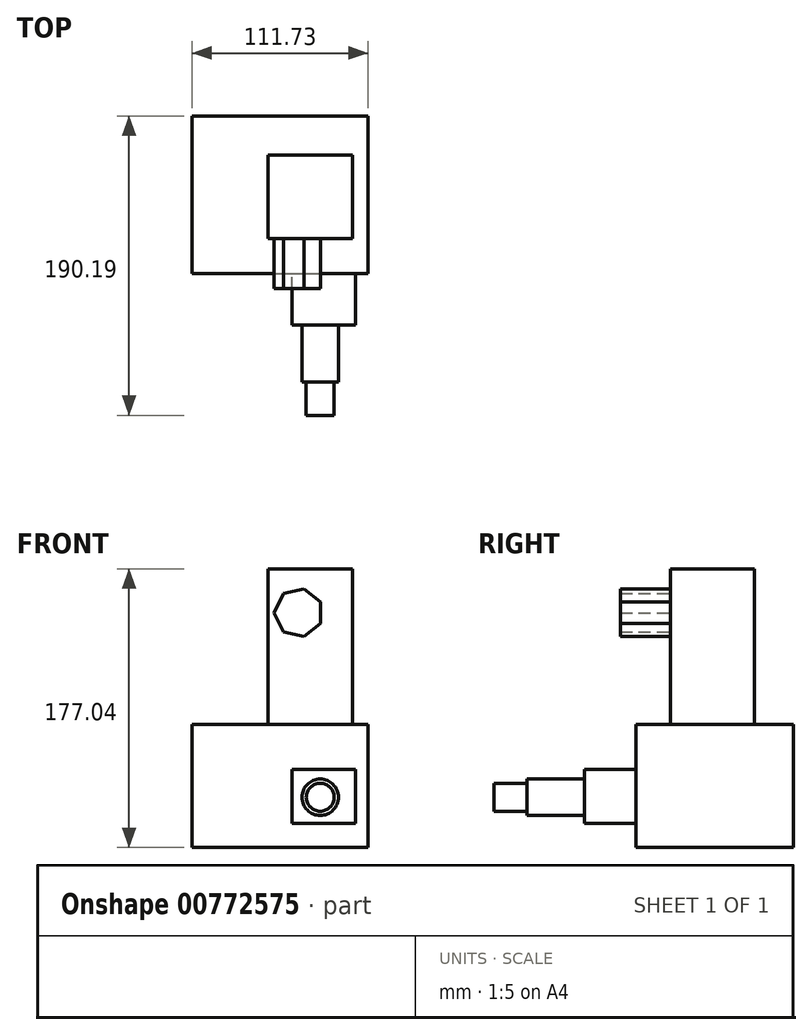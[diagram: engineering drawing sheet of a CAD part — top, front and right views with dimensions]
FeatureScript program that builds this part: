
annotation { "Feature Type Name" : "Feature", "Feature Type Description" : "" }
export const myFeature = defineFeature(function(context is Context, id is Id, definition is map)
    precondition{}
    {
        {
            var Q0;
            Q0=qCreatedBy(makeId("Top.planeOp"),FACE);
            var sketch = newSketch(context, id + "F0", { "sketchPlane" : qUnion([Q0])});
            skLineSegment(sketch, "E0.bottom", {"start": v(-56.46, -33.14) * mm, "end": v(55.27, -33.14) * mm});
            skLineSegment(sketch, "E0.top", {"start": v(-56.46, 66.88) * mm, "end": v(55.27, 66.88) * mm});
            skLineSegment(sketch, "E0.left", {"start": v(-56.46, -33.14) * mm, "end": v(-56.46, 66.88) * mm});
            skLineSegment(sketch, "E0.right", {"start": v(55.27, -33.14) * mm, "end": v(55.27, 66.88) * mm});
            skSolve(sketch);
        }
        {
            var Q0;
            Q0 = qSketchRegion(id + "F0", true);
            extrude(context, id + "F1", {"entities" : qUnion([Q0]), "depth" : 78.23 * mm, "offsetDistance" : 25.4 * mm});
        }
        {
            var Q0;
            Q0=makeQuery(id+"F1.opExtrude","SWEPT_FACE",FACE,{"disambiguationData":[OSD([sQuery(id+"F0.wireOp",EDGE,"E0.bottom")])]});
            var sketch = newSketch(context, id + "F2", { "sketchPlane" : qUnion([Q0])});
            skLineSegment(sketch, "E1.bottom", {"start": v(7.16, 49.63) * mm, "end": v(47.4, 49.63) * mm});
            skLineSegment(sketch, "E1.top", {"start": v(7.16, 15.5) * mm, "end": v(47.4, 15.5) * mm});
            skLineSegment(sketch, "E1.left", {"start": v(7.16, 49.63) * mm, "end": v(7.16, 15.5) * mm});
            skLineSegment(sketch, "E1.right", {"start": v(47.4, 49.63) * mm, "end": v(47.4, 15.5) * mm});
            skSolve(sketch);
        }
        {
            var Q0;
            Q0 = qSketchRegion(id + "F2", true);
            extrude(context, id + "F3", {"entities" : qUnion([Q0]), "operationType" : NewBodyOperationType.ADD, "depth" : 32.77 * mm, "offsetDistance" : 25.4 * mm});
        }
        {
            var Q0;
            Q0=makeQuery(id+"F3.opExtrude","CAP_FACE",FACE,{"disambiguationData":[OSD([sQuery(id+"F2.wireOp",EDGE,"E1.bottom"),sQuery(id+"F2.wireOp",EDGE,"E1.top"),sQuery(id+"F2.wireOp",EDGE,"E1.left"),sQuery(id+"F2.wireOp",EDGE,"E1.right")])],"isStart":false});
            var sketch = newSketch(context, id + "F4", { "sketchPlane" : qUnion([Q0])});
            skCircle(sketch, "E2", {"center": v(24.92, 31.95) * mm, "radius": 11.57 * mm});
            skSolve(sketch);
        }
        {
            var Q0;
            Q0 = qSketchRegion(id + "F4", true);
            extrude(context, id + "F5", {"entities" : qUnion([Q0]), "operationType" : NewBodyOperationType.ADD, "depth" : 36.32 * mm, "offsetDistance" : 25.4 * mm});
        }
        {
            var Q0;
            Q0=makeQuery(id+"F5.opExtrude","CAP_FACE",FACE,{"disambiguationData":[OSD([sQuery(id+"F4.wireOp",EDGE,"E2")])],"isStart":false});
            var sketch = newSketch(context, id + "F6", { "sketchPlane" : qUnion([Q0])});
            skCircle(sketch, "E3", {"center": v(24.92, 31.95) * mm, "radius": 8.88 * mm});
            skSolve(sketch);
        }
        {
            var Q0;
            Q0 = qSketchRegion(id + "F6", true);
            extrude(context, id + "F7", {"entities" : qUnion([Q0]), "operationType" : NewBodyOperationType.ADD, "depth" : 21.08 * mm, "offsetDistance" : 25.4 * mm});
        }
        {
            var Q0;
            Q0=makeQuery(id+"F1.opExtrude","CAP_FACE",FACE,{"disambiguationData":[OSD([sQuery(id+"F0.wireOp",EDGE,"E0.bottom"),sQuery(id+"F0.wireOp",EDGE,"E0.top"),sQuery(id+"F0.wireOp",EDGE,"E0.left"),sQuery(id+"F0.wireOp",EDGE,"E0.right")])],"isStart":false});
            var sketch = newSketch(context, id + "F8", { "sketchPlane" : qUnion([Q0])});
            skLineSegment(sketch, "E4.bottom", {"start": v(-8.07, 42) * mm, "end": v(45.48, 42) * mm});
            skLineSegment(sketch, "E4.top", {"start": v(-8.07, -11.15) * mm, "end": v(45.48, -11.15) * mm});
            skLineSegment(sketch, "E4.left", {"start": v(-8.07, 42) * mm, "end": v(-8.07, -11.15) * mm});
            skLineSegment(sketch, "E4.right", {"start": v(45.48, 42) * mm, "end": v(45.48, -11.15) * mm});
            skSolve(sketch);
        }
        {
            var Q0;
            Q0 = qSketchRegion(id + "F8", true);
            extrude(context, id + "F9", {"entities" : qUnion([Q0]), "operationType" : NewBodyOperationType.ADD, "depth" : 38.86 * mm, "offsetDistance" : 25.4 * mm});
        }
        {
            var Q0;
            Q0=makeQuery(id+"F9.opExtrude","CAP_FACE",FACE,{"disambiguationData":[OSD([sQuery(id+"F8.wireOp",EDGE,"E4.bottom"),sQuery(id+"F8.wireOp",EDGE,"E4.top"),sQuery(id+"F8.wireOp",EDGE,"E4.left"),sQuery(id+"F8.wireOp",EDGE,"E4.right")])],"isStart":false});
            extrude(context, id + "F10", {"entities" : qUnion([Q0]), "operationType" : NewBodyOperationType.ADD, "depth" : 59.94 * mm, "offsetDistance" : 25.4 * mm});
        }
        {
            var Q0;
            {var subQ0=sQuery(id+"F8.wireOp",EDGE,"E4.top");Q0=makeQuery(id+"F10.boolean.opBoolean","MERGE",FACE,{"derivedFrom":[makeQuery(id+"F9.opExtrude","SWEPT_FACE",FACE,{"disambiguationData":[OSD([subQ0])]}),makeQuery(id+"F10.opExtrude","SWEPT_FACE",FACE,{"disambiguationData":[OSD([subQ0])]})]});}
            var sketch = newSketch(context, id + "F11", { "sketchPlane" : qUnion([Q0])});
            skCircle(sketch, "E5.cCircle", {"center": v(11.25, 149.13) * mm, "radius": 14 * mm, "construction": true});
            skLineSegment(sketch, "E5.0", {"start": v(25.24, 155.87) * mm, "end": v(25.24, 142.4) * mm});
            skLineSegment(sketch, "E5.1", {"start": v(25.24, 142.4) * mm, "end": v(14.7, 133.99) * mm});
            skLineSegment(sketch, "E5.2", {"start": v(14.7, 133.99) * mm, "end": v(1.56, 136.99) * mm});
            skLineSegment(sketch, "E5.3", {"start": v(1.56, 136.99) * mm, "end": v(-4.29, 149.13) * mm});
            skLineSegment(sketch, "E5.4", {"start": v(-4.29, 149.13) * mm, "end": v(1.56, 161.28) * mm});
            skLineSegment(sketch, "E5.5", {"start": v(1.56, 161.28) * mm, "end": v(14.7, 164.28) * mm});
            skLineSegment(sketch, "E5.6", {"start": v(14.7, 164.28) * mm, "end": v(25.24, 155.87) * mm});
            skPoint(sketch, "E5.0.midPoint", {"position": v(25.24, 149.13) * mm});
            skSolve(sketch);
        }
        {
            var Q0;
            Q0 = qSketchRegion(id + "F11", true);
            extrude(context, id + "F12", {"entities" : qUnion([Q0]), "operationType" : NewBodyOperationType.ADD, "depth" : 31.75 * mm, "offsetDistance" : 25.4 * mm});
        }
    });
